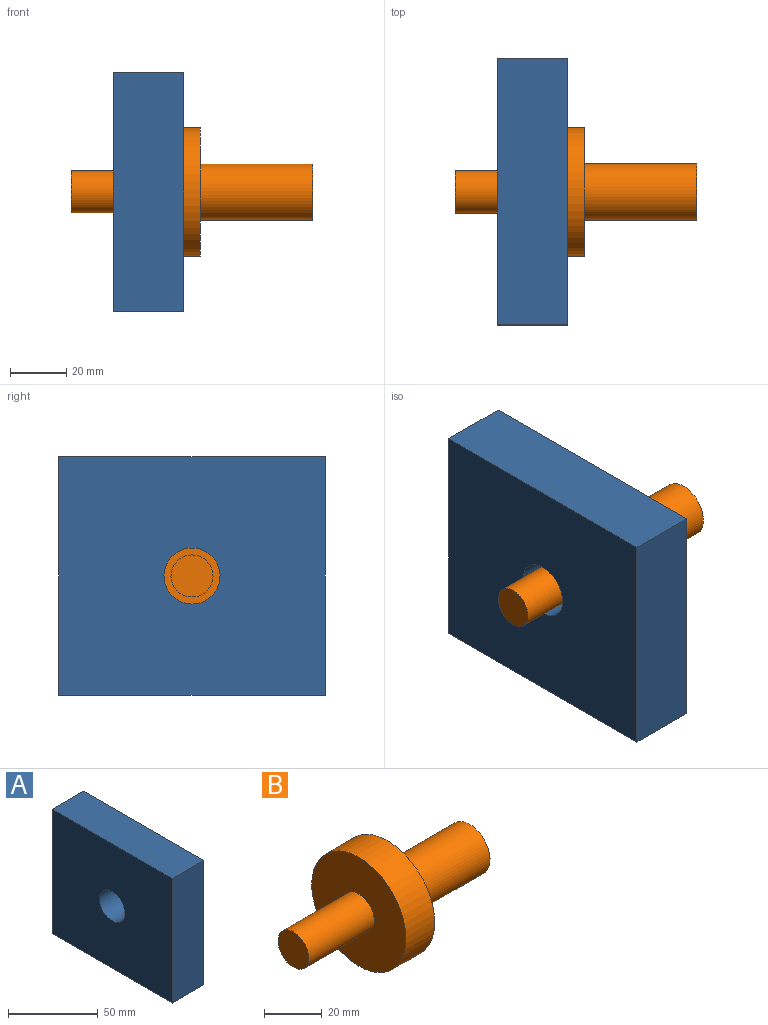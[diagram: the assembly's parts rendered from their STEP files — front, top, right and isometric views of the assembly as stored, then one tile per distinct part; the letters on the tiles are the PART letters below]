
ASSEMBLY  parts=2 mates=1
PART A: 9 faces, bbox 25x95x85 mm
  f0: cylinder r=10mm len=20mm, axis (1,0,0), area 1068.1mm2, adj f6,f8
  f1: plane 85x25mm, normal (0,1,0), area 2125mm2, adj f2,f4,f5,f6
  f2: plane 95x25mm, normal (0,0,1), area 2375mm2, adj f1,f3,f5,f6
  f3: plane 85x25mm, normal (0,-1,0), area 2125mm2, adj f2,f4,f5,f6
  f4: plane 95x25mm, normal (0,0,-1), area 2375mm2, adj f1,f3,f5,f6
  f5: plane 95x85mm, normal (1,0,0), area 6413.1mm2, adj f1,f2,f3,f4,f7
  f6: plane 95x85mm, normal (-1,0,0), area 7760.8mm2, adj f0,f1,f2,f3,f4
  f7: cylinder r=23mm len=46mm, axis (1,0,0), area 1156.1mm2, adj f5,f8
  f8: plane 46x46mm, normal (1,0,0), area 1347.7mm2, adj f0,f7
PART B: 7 faces, bbox 86x46x46 mm
  f0: cylinder r=23mm len=46mm, axis (-1,0,0), area 2023.2mm2, adj f1,f2
  f1: plane 46x46mm, normal (1,0,0), area 1347.7mm2, adj f0,f3
  f2: plane 46x46mm, normal (-1,0,0), area 1485.2mm2, adj f0,f5
  f3: cylinder r=10mm len=40mm, axis (-1,0,0), area 2513.3mm2, adj f1,f4
  f4: plane 20x20mm, normal (1,0,0), area 314.2mm2, adj f3
  f5: cylinder r=7.5mm len=32mm, axis (1,0,0), area 1508mm2, adj f2,f6
  f6: plane 15x15mm, normal (-1,0,0), area 176.7mm2, adj f5
PLACE A t=(59.88,31.69,9.23)mm
PLACE B t=(76.88,31.69,9.23)mm
MATE slider A.f7 <-> B.f0  axis (1,0,0) through (76.88,31.69,9.23)mm
